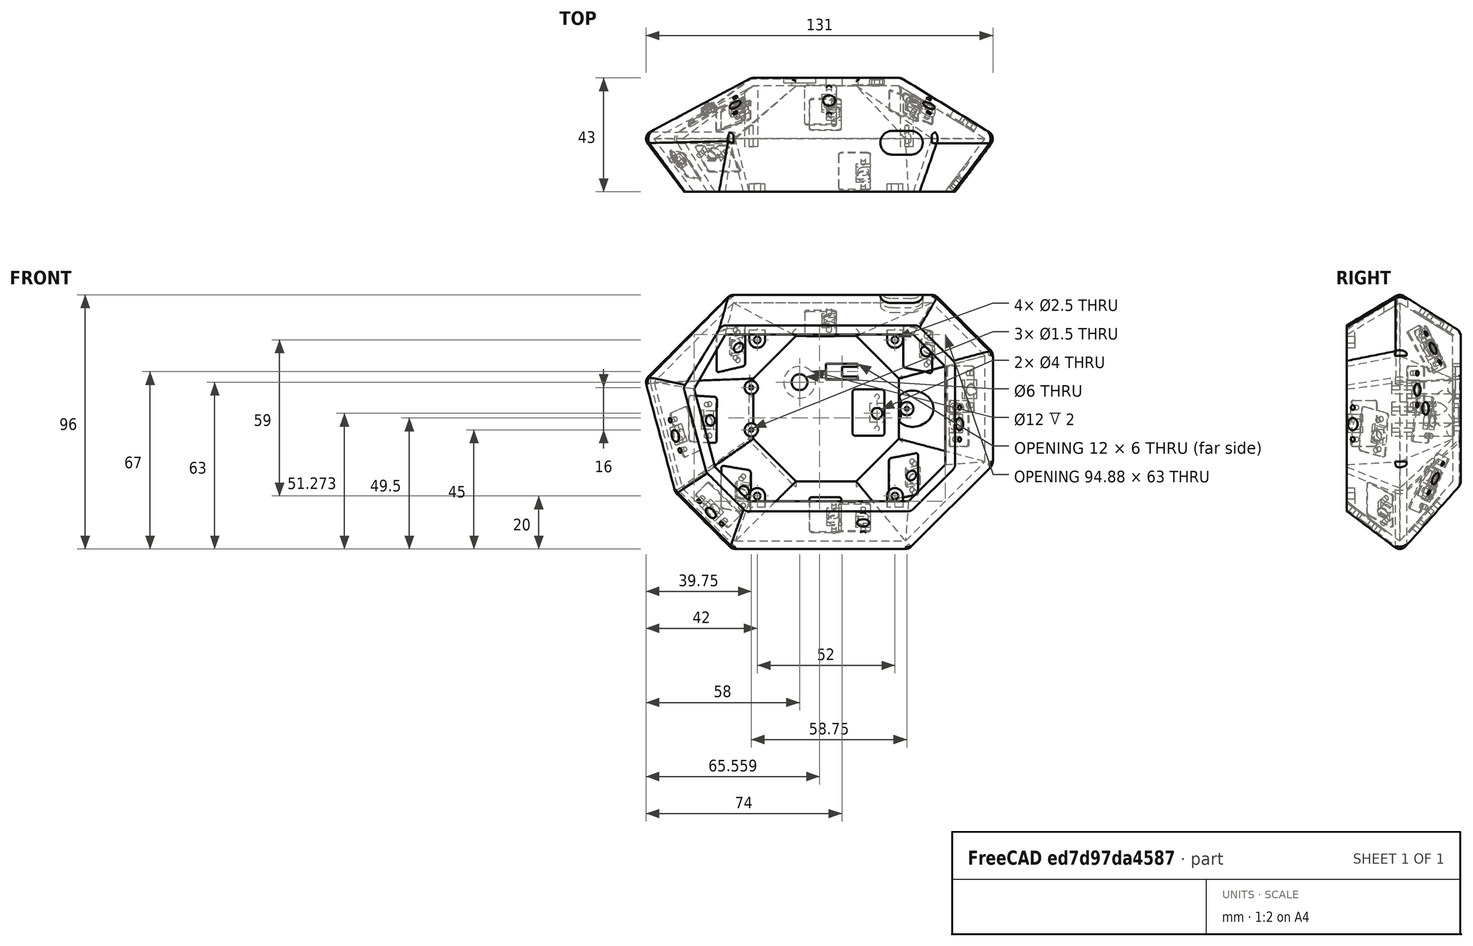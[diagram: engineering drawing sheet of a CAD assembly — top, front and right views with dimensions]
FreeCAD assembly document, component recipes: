
FREECAD ASSEMBLY — COMPONENT RECIPES ("tracker-tut")

This assembly document has 17 components, labeled P0..P16 below (a component is one placed body or linked part). 16 of them carry a construction recipe — the FreeCAD feature program that regenerates the part from scratch, quoted from this document or its linked companion documents; the rest are supplied as boundary geometry only. No exploded tour is included for this assembly.
COMPONENT P0 — recipe-attached ("Tracker final", modeled in this document).
Construction recipe (the document's own serialized feature program — sketch geometry with constraints, then the solid features built on it; lengths are millimeters unless a unit is written):

FEATURE [PartDesign::FeatureBase] BaseFeature
  BaseFeature = -> cut_obj
FEATURE [PartDesign::Plane] DatumPlane002
  AttachmentOffset = pos=(0,0,-17) rot=(0,0,1;0rad)
  Length = 153.4
  MapMode = 5
  Placement = pos=(0,17,3.8e-15) rot=(1,0,0;1.5708rad)
  ResizeMode = 0
  Support = -> [XZ_Plane001]
  Width = 118.409
FEATURE [Sketcher::SketchObject] Sketch003
  FullyConstrained = true
  MapMode = 5
  Placement = pos=(0,17,3.8e-15) rot=(1,0,0;1.5708rad)
  Support = -> [DatumPlane002]
  sketch-geometry (3):
    g0: Circle CenterX=-28.25 CenterY=8 CenterZ=0 NormalX=0 NormalY=0 NormalZ=1 AngleXU=0 Radius=2.5
    g1: Circle CenterX=-28.25 CenterY=-8 CenterZ=0 NormalX=0 NormalY=0 NormalZ=1 AngleXU=0 Radius=2.5
    g2: Circle CenterX=30.5 CenterY=0 CenterZ=0 NormalX=0 NormalY=0 NormalZ=1 AngleXU=0 Radius=2.5
  constraints (9):
    c: PointOnObject(g2,g-1)
    c: DistanceX(g0) = -28.25
    c: DistanceY(g0) = 8
    c: DistanceY(g1,g0) = 16
    c: DistanceX(g0,g2) = 58.75
    c: Equal(g0,g1)
    c: Equal(g1,g2)
    c: Diameter(g0) = 5
    c: Vertical(g1,g0)
FEATURE [PartDesign::Pad] Pad
  BaseFeature = -> BaseFeature
  Direction = (0,-1,-2e-16)
  Length = 18
  Length2 = 10
  Profile = -> Sketch003
  ReferenceAxis = -> Sketch003 [N_Axis]
  Reversed = true
  Type = 2
FEATURE [Sketcher::SketchObject] Sketch004
  FullyConstrained = true
  MapMode = 5
  Placement = pos=(0,17,3.8e-15) rot=(1,0,0;1.5708rad)
  Support = -> [DatumPlane002]
  sketch-geometry (3):
    g0: Circle CenterX=-28.25 CenterY=8 CenterZ=0 NormalX=0 NormalY=0 NormalZ=1 AngleXU=0 Radius=1
    g1: Circle CenterX=-28.25 CenterY=-8 CenterZ=0 NormalX=0 NormalY=0 NormalZ=1 AngleXU=0 Radius=1
    g2: Circle CenterX=30.5 CenterY=0 CenterZ=0 NormalX=0 NormalY=0 NormalZ=1 AngleXU=0 Radius=1
  constraints (9):
    c: PointOnObject(g2,g-1)
    c: DistanceX(g0) = -28.25
    c: DistanceY(g0) = 8
    c: DistanceY(g1,g0) = 16
    c: DistanceX(g2) = 30.5
    c: Equal(g0,g1)
    c: Equal(g0,g2)
    c: Diameter(g0) = 2
    c: Vertical(g1,g0)
FEATURE [PartDesign::Hole] Hole
  BaseFeature = -> Pad
  CustomThreadClearance = 0
  Depth = 8
  DepthType = 0
  Diameter = 1.5
  DrillForDepth = false
  DrillPoint = 1
  DrillPointAngle = 118
  HoleCutCountersinkAngle = 90
  HoleCutCustomValues = false
  HoleCutDepth = 0
  HoleCutDiameter = 6.1
  HoleCutType = 0
  ModelThread = false
  Profile = -> Sketch004
  Tapered = false
  TaperedAngle = 90
  ThreadClass = 0
  ThreadDepth = 8
  ThreadDepthType = 0
  ThreadDirection = 0
  ThreadFit = 0
  ThreadSize = 0
  ThreadType = 0
  Threaded = false
  UseCustomThreadClearance = false
FEATURE [Sketcher::SketchObject] Sketch005
  AttachmentOffset = pos=(0,0,6) rot=(0,0,1;0rad)
  FullyConstrained = true
  MapMode = 5
  Placement = pos=(0,0,6) rot=(0,0,1;0rad)
  Support = -> [XY_Plane001]
  sketch-geometry (4):
    g0: ArcOfCircle CenterX=25 CenterY=18.5 CenterZ=0 NormalX=0 NormalY=0 NormalZ=1 AngleXU=0 Radius=4.5 StartAngle=1.5708 EndAngle=4.71239
    g1: ArcOfCircle CenterX=32 CenterY=18.5 CenterZ=0 NormalX=0 NormalY=0 NormalZ=1 AngleXU=0 Radius=4.5 StartAngle=4.71239 EndAngle=7.85398
    g2: LineSegment StartX=25 StartY=14 StartZ=0 EndX=32 EndY=14 EndZ=0
    g3: LineSegment StartX=32 StartY=23 StartZ=0 EndX=25 EndY=23 EndZ=0
  constraints (10):
    c: Tangent(g0,g2) = -1.5708
    c: Tangent(g2,g1) = -1.5708
    c: Tangent(g1,g3) = -1.5708
    c: Tangent(g3,g0) = -1.5708
    c: Equal(g0,g1)
    c: Horizontal(g2)
    c: DistanceX(g0) = 25
    c: DistanceY(g0) = 18.5
    c: DistanceX(g0,g1) = 7
    c: Radius(g1) = 4.5
FEATURE [PartDesign::Pocket] Pocket
  BaseFeature = -> Hole
  Direction = (0,0,-1)
  Length = 5
  Length2 = 5
  Profile = -> Sketch005
  ReferenceAxis = -> Sketch005 [N_Axis]
  Reversed = true
  Type = 1
FEATURE [Sketcher::SketchObject] Sketch006
  FullyConstrained = true
  MapMode = 5
  Placement = pos=(0,43,0) rot=(0,0.707107,0.707107;3.14159rad)
  Support = -> [Pocket]
  sketch-geometry (1):
    g0: Circle CenterX=10 CenterY=10 CenterZ=0 NormalX=0 NormalY=0 NormalZ=1 AngleXU=0 Radius=6
  constraints (3):
    c: DistanceX(g0) = 10
    c: DistanceY(g0) = 10
    c: Diameter(g0) = 12
FEATURE [PartDesign::Hole] Hole001
  BaseFeature = -> Pocket
  CustomThreadClearance = 0
  Depth = 5
  DepthType = 0
  Diameter = 6
  DrillForDepth = false
  DrillPoint = 1
  DrillPointAngle = 118
  HoleCutCountersinkAngle = 90
  HoleCutCustomValues = false
  HoleCutDepth = 2
  HoleCutDiameter = 12
  HoleCutType = 1
  ModelThread = false
  Profile = -> Sketch006
  Tapered = false
  TaperedAngle = 90
  ThreadClass = 0
  ThreadDepth = 5
  ThreadDepthType = 0
  ThreadDirection = 0
  ThreadFit = 0
  ThreadSize = 0
  ThreadType = 0
  Threaded = false
  UseCustomThreadClearance = false
FEATURE [Sketcher::SketchObject] Sketch007
  FullyConstrained = true
  MapMode = 5
  Placement = pos=(0,43,0) rot=(0,0.707107,0.707107;3.14159rad)
  Support = -> [Hole001]
  sketch-geometry (8):
    g0: LineSegment StartX=-12 StartY=17 StartZ=0 EndX=0 EndY=17 EndZ=0
    g1: LineSegment StartX=0 StartY=17 StartZ=0 EndX=0 EndY=11 EndZ=0
    g2: LineSegment StartX=0 StartY=11 StartZ=0 EndX=-12 EndY=11 EndZ=0
    g3: LineSegment StartX=-12 StartY=11 StartZ=0 EndX=-12 EndY=12.2 EndZ=0
    g4: LineSegment StartX=-12 StartY=12.2 StartZ=0 EndX=-6 EndY=12.2 EndZ=0
    g5: LineSegment StartX=-6 StartY=12.2 StartZ=0 EndX=-6 EndY=15.8 EndZ=0
    g6: LineSegment StartX=-6 StartY=15.8 StartZ=0 EndX=-12 EndY=15.8 EndZ=0
    g7: LineSegment StartX=-12 StartY=15.8 StartZ=0 EndX=-12 EndY=17 EndZ=0
  constraints (24):
    c: Horizontal(g0)
    c: Coincident(g0,g1)
    c: Coincident(g1,g2)
    c: Horizontal(g2)
    c: Coincident(g2,g3)
    c: Vertical(g3)
    c: Coincident(g3,g4)
    c: Horizontal(g4)
    c: Coincident(g4,g5)
    c: Vertical(g5)
    c: Coincident(g5,g6)
    c: Horizontal(g6)
    c: Coincident(g6,g7)
    c: Coincident(g7,g0)
    c: Vertical(g7)
    c: Vertical(g1)
    c: DistanceY(g1,g1) = 6
    c: Equal(g7,g3)
    c: DistanceY(g3,g3) = 1.2
    c: DistanceX(g4,g1) = 6
    c: DistanceX(g2,g2) = 12
    c: Vertical(g3,g6)
    c: DistanceX(g1) = 0
    c: DistanceY(g1) = 11
FEATURE [PartDesign::Pocket] Pocket001
  BaseFeature = -> Hole001
  Direction = (0,-1,-2e-16)
  Length = 5
  Length2 = 5
  Profile = -> Sketch007
  ReferenceAxis = -> Sketch007 [N_Axis]
  Type = 0
FEATURE [Sketcher::SketchObject] Sketch008
  FullyConstrained = true
  MapMode = 5
  Placement = pos=(0,0,0) rot=(1,0,0;1.5708rad)
  Support = -> [XZ_Plane001]
  sketch-geometry (10):
    g0: ArcOfCircle CenterX=-26 CenterY=26 CenterZ=0 NormalX=0 NormalY=0 NormalZ=1 AngleXU=0 Radius=3 StartAngle=3.14159 EndAngle=6.28319
    g1: LineSegment StartX=-29 StartY=26 StartZ=0 EndX=-29 EndY=31 EndZ=0
    g2: LineSegment StartX=-29 StartY=31 StartZ=0 EndX=-23 EndY=31 EndZ=0
    g3: LineSegment StartX=-23 StartY=31 StartZ=0 EndX=-23 EndY=26 EndZ=0
    g4: Circle CenterX=-26 CenterY=26 CenterZ=0 NormalX=0 NormalY=0 NormalZ=1 AngleXU=0 Radius=1.25
    g5: Circle CenterX=-26 CenterY=-33 CenterZ=0 NormalX=0 NormalY=0 NormalZ=1 AngleXU=0 Radius=1.25
    g6: ArcOfCircle CenterX=-26 CenterY=-33 CenterZ=0 NormalX=0 NormalY=0 NormalZ=1 AngleXU=0 Radius=3 StartAngle=5.6e-15 EndAngle=3.14159
    g7: LineSegment StartX=-29 StartY=-33 StartZ=0 EndX=-29 EndY=-38 EndZ=0
    g8: LineSegment StartX=-29 StartY=-38 StartZ=0 EndX=-23 EndY=-38 EndZ=0
    g9: LineSegment StartX=-23 StartY=-38 StartZ=0 EndX=-23 EndY=-33 EndZ=0
  constraints (26):
    c: Vertical(g1)
    c: Coincident(g1,g2)
    c: Horizontal(g2)
    c: Coincident(g2,g3)
    c: Vertical(g3)
    c: Tangent(g0,g3) = 1.5708
    c: Tangent(g0,g1) = 1.5708
    c: Coincident(g4,g0)
    c: Diameter(g4) = 2.5
    c: Radius(g0) = 3
    c: DistanceX(g0) = -26
    c: DistanceY(g0) = 26
    c: DistanceY(g0,g2) = 5
    c: Coincident(g6,g5)
    c: Coincident(g7,g8)
    c: Horizontal(g8)
    c: Coincident(g8,g9)
    c: Equal(g5,g4)
    c: Equal(g6,g0)
    c: Vertical(g7)
    c: Vertical(g9)
    c: Tangent(g6,g9) = -1.5708
    c: Vertical(g5,g0)
    c: DistanceY(g5) = -33
    c: Tangent(g6,g7) = -1.5708
    c: DistanceY(g8,g5) = 5
FEATURE [PartDesign::Pad] Pad001
  BaseFeature = -> Pocket001
  Direction = (0,-1,-2e-16)
  Length = 3
  Length2 = 10
  Profile = -> Sketch008
  ReferenceAxis = -> Sketch008 [N_Axis]
  Refine = true
  Reversed = true
  Type = 0
FEATURE [PartDesign::Mirrored] Mirrored
  BaseFeature = -> Pad001
  MirrorPlane = -> Sketch008 [V_Axis]
  Originals = -> [Pad001]
  Refine = true
FEATURE [PartDesign::Fillet] Fillet
  Base = -> Mirrored [Edge455]
  BaseFeature = -> Mirrored
  Radius = 5
  SupportTransform = false
  UseAllEdges = false
FEATURE [PartDesign::Body] Body001  label="Tracker final"
  BaseFeature = -> cut_obj
  Group = -> [BaseFeature,DatumPlane002,Sketch003,Pad,Sketch004,Hole,Sketch005,Pocket,Sketch006,Hole001,Sketch007,Pocket001,Sketch008,Pad001,Mirrored,Fillet]
  Origin = -> Origin001
  Tip = -> Fillet
COMPONENT P1 — geometry summary ("tracker-mainboard"; no construction recipe available for this part):
  bounding box: 71.5 x 44.8 x 11.5 mm
  tessellated surface: 104,766 triangles
  volume: 4982 mm^3 (13% of its bounding box)
COMPONENT P2 — recipe-attached ("sensor", a linked part whose construction recipe lives in a companion FreeCAD document of the same project; that document's serialized recipe follows).
Construction recipe (the companion document, serialized — sketch geometry with constraints, then the solid features built on it; lengths are millimeters unless a unit is written):

FCSTD DOCUMENT  (FreeCAD 0.20R29603 (Git))
Label: sensor-PCB
License: All rights reserved
LicenseURL: http://en.wikipedia.org/wiki/All_rights_reserved
objects: Part::Feature×21, App::Part×16, App::Link×15, Part::Compound2×3, PartDesign::SubShapeBinder×2, PartDesign::CoordinateSystem×2, App::FeaturePython×1, PartDesign::Body×1
note: 26 computed .brp shape members not serialized (recipe doc carries the construction recipe); baked Part::Feature solids carry a one-line shape summary decoded from their .brp

FEATURE [App::FeaturePython] Constraints  # WARN: FeaturePython — macro-defined, semantics opaque (R4)
  _Version = 1
FEATURE [App::Link] Link  label="ball001"
  LinkPlacement = pos=(0,0.5,0.125) rot=(0,0,1;0rad)
  LinkedObject = -> Solid002
  Placement = pos=(0,0.5,0.125) rot=(0,0,1;0rad)
FEATURE [App::Link] Link001  label="ball002"
  LinkPlacement = pos=(0.5,0.5,0.125) rot=(0,0,1;0rad)
  LinkedObject = -> Solid002
  Placement = pos=(0.5,0.5,0.125) rot=(0,0,1;0rad)
FEATURE [App::Link] Link002  label="ball003"
  LinkPlacement = pos=(-0.5,0,0.125) rot=(0,0,1;0rad)
  LinkedObject = -> Solid002
  Placement = pos=(-0.5,0,0.125) rot=(0,0,1;0rad)
FEATURE [App::Link] Link003  label="ball004"
  LinkPlacement = pos=(0,0,0.125) rot=(0,0,1;0rad)
  LinkedObject = -> Solid002
  Placement = pos=(0,0,0.125) rot=(0,0,1;0rad)
FEATURE [App::Link] Link004  label="ball005"
  LinkPlacement = pos=(0.5,0,0.125) rot=(0,0,1;0rad)
  LinkedObject = -> Solid002
  Placement = pos=(0.5,0,0.125) rot=(0,0,1;0rad)
FEATURE [App::Link] Link005  label="ball006"
  LinkPlacement = pos=(-0.5,-0.5,0.125) rot=(0,0,1;0rad)
  LinkedObject = -> Solid002
  Placement = pos=(-0.5,-0.5,0.125) rot=(0,0,1;0rad)
FEATURE [App::Link] Link006  label="ball007"
  LinkPlacement = pos=(0,-0.5,0.125) rot=(0,0,1;0rad)
  LinkedObject = -> Solid002
  Placement = pos=(0,-0.5,0.125) rot=(0,0,1;0rad)
FEATURE [App::Link] Link007  label="ball008"
  LinkPlacement = pos=(0.5,-0.5,0.125) rot=(0,0,1;0rad)
  LinkedObject = -> Solid002
  Placement = pos=(0.5,-0.5,0.125) rot=(0,0,1;0rad)
FEATURE [App::Link] Link008  label="Terminal001"
  LinkPlacement = pos=(1.2,0.45,0) rot=(0,0,1;3.14159rad)
  LinkedObject = -> Part004
  Placement = pos=(1.2,0.45,0) rot=(0,0,1;3.14159rad)
FEATURE [App::Link] Link009  label="68X1XX183X22_Pin_TOP001"
  LinkPlacement = pos=(-0.4,1.05,-0.045) rot=(0,0,1;1.5708rad)
  LinkedObject = -> Solid010
  Placement = pos=(-0.4,1.05,-0.045) rot=(0,0,1;1.5708rad)
FEATURE [App::Link] Link010  label="68X1XX183X22_Pin_TOP002"
  LinkPlacement = pos=(0.6,1.05,-0.045) rot=(0,0,1;1.5708rad)
  LinkedObject = -> Solid010
  Placement = pos=(0.6,1.05,-0.045) rot=(0,0,1;1.5708rad)
FEATURE [App::Link] Link011  label="68X1XX183X22_Pin_TOP003"
  LinkPlacement = pos=(1.6,1.05,-0.045) rot=(0,0,1;1.5708rad)
  LinkedObject = -> Solid010
  Placement = pos=(1.6,1.05,-0.045) rot=(0,0,1;1.5708rad)
FEATURE [App::Link] Link012  label="pin001"
  LinkPlacement = pos=(0.375,3e-16,-3e-16) rot=(0,0,1;3.14159rad)
  LinkedObject = -> Solid019
  Placement = pos=(0.375,3e-16,-3e-16) rot=(0,0,1;3.14159rad)
FEATURE [App::Link] Link013  label="1x0.5x0.5x0.026"
  LinkPlacement = pos=(4.25098,5.93,0) rot=(0,0,-1;1.5708rad)
  LinkedObject = -> Part011
  Placement = pos=(4.25098,5.93,0) rot=(0,0,-1;1.5708rad)
FEATURE [App::Link] Link014  label="1x0.5x0.5x0.027"
  LinkPlacement = pos=(4.88605,11.5101,0) rot=(0,0,1;0rad)
  LinkedObject = -> Part011
  Placement = pos=(4.88605,11.5101,0) rot=(0,0,1;0rad)
FEATURE [App::Part] Part013  label="C2"
  Group = -> [Link013]
  Origin = -> Origin013
FEATURE [App::Part] Part015  label="C1"
  Group = -> [Link014]
  Origin = -> Origin015
FEATURE [Part::Feature] Shell  label="Open_CASCADE_STEP_translator_6.8_1.1"
  Placement = pos=(-0.81,-0.79,0) rot=(0,0,1;0rad)
  shape: bbox 0.2025 x 0.2025 x 2e-07 mm, 1 faces, 0 solids (baked)
FEATURE [Part::Feature] Solid  label="Open CASCADE STEP translator 6.8 2.1.1"
  Placement = pos=(0,0,-1.54144) rot=(0,0,1;0rad)
  shape: bbox 11.5 x 17 x 1.541 mm, 14 faces (baked)
FEATURE [App::Part] Part  label="Board"
  Group = -> [Solid]
  Origin = -> Origin
FEATURE [Part::Feature] Solid001  label="Open_CASCADE_STEP_translator_6.8_1.2.1"
  shape: bbox 1.62 x 1.58 x 0.475 mm, 8 faces (baked)
FEATURE [App::Part] Part001  label="Body"
  Group = -> [Solid001]
  Origin = -> Origin001
  Placement = pos=(-0.81,-0.79,0) rot=(0,0,1;0rad)
FEATURE [Part::Feature] Solid002  label="ball"
  Placement = pos=(-0.5,0.5,0.125) rot=(0,0,1;0rad)
  shape: bbox 0.25 x 0.25 x 0.25 mm, 1 faces (baked)
FEATURE [App::Part] Part002  label="5833252656"
  Group = -> [Shell,Part001,Solid002,Link,Link001,Link002,Link003,Link004,Link005,Link006,Link007]
  Origin = -> Origin002
  Placement = pos=(4.878,8.47,0) rot=(0,0,1;1.5708rad)
FEATURE [App::Part] Part003  label="U1"
  Group = -> [Part002]
  Origin = -> Origin003
FEATURE [Part::Feature] Solid003  label="Mid_Body"
  Placement = pos=(-1.2,-0.45,0) rot=(0,0,1;0rad)
  shape: bbox 2.28 x 0.9 x 0.48 mm, 6 faces (baked)
FEATURE [Part::Feature] Solid004  label="Open_CASCADE_STEP_translator_6.8_3.2.1"
  shape: bbox 0.7 x 0.9 x 0.6 mm, 10 faces (baked)
FEATURE [App::Part] Part004  label="Terminal"
  Group = -> [Solid004]
  Origin = -> Origin004
  Placement = pos=(-1.2,-0.45,0) rot=(0,0,1;0rad)
FEATURE [Part::Feature] Solid005  label="Mark"
  Placement = pos=(-0.5,-0.45,0.54) rot=(0,0,1;0rad)
  shape: bbox 1 x 0.9 x 0.06 mm, 6 faces (baked)
FEATURE [App::Part] Part005  label="5983538608"
  Group = -> [Solid003,Part004,Link008,Solid005]
  Origin = -> Origin005
  Placement = pos=(5.6,5.5,0) rot=(0,0,1;1.5708rad)
FEATURE [App::Part] Part006  label="R1"
  Group = -> [Part005]
  Origin = -> Origin006
FEATURE [Part::Feature] Solid006  label="68x109183x22"
  shape: bbox 7.5 x 3.1 x 1.2 mm, 237 faces (baked)
FEATURE [Part::Feature] Solid007  label="68x109183x22_Actuator"
  Placement = pos=(-1.67e-13,-2,5e-15) rot=(1,0,0;3.14159rad)
  shape: bbox 10.2 x 3.8 x 1.1 mm, 117 faces (baked)
FEATURE [Part::Feature] Solid008  label="68X1xx183x22_Solder_Pad2"
  Placement = pos=(2.8,-0.25,-0.02) rot=(0,0,-1;1.5708rad)
  shape: bbox 2 x 2.5 x 1.24 mm, 61 faces (baked)
FEATURE [Part::Feature] Solid009  label="68X1XX183X22_Solder_Pad"
  Placement = pos=(-2.8,-0.25,-0.02) rot=(0.707107,-0.707107,0;3.14159rad)
  shape: bbox 2 x 2.5 x 1.24 mm, 61 faces (baked)
FEATURE [Part::Feature] Solid010  label="68X1XX183X22_Pin_TOP"
  Placement = pos=(-1.4,1.05,-0.045) rot=(0,0,1;1.5708rad)
  shape: bbox 0.2 x 3.097 x 1.15 mm, 38 faces (baked)
FEATURE [App::Part] Part007  label="686104183422"
  Group = -> [Solid006,Solid007,Solid008,Solid009,Solid010,Link009,Link010,Link011]
  Origin = -> Origin007
  Placement = pos=(8.95005,8.49992,0.640001) rot=(0.707107,-0.707107,0;3.14159rad)
FEATURE [App::Part] Part008  label="J1"
  Group = -> [Part007]
  Origin = -> Origin008
FEATURE [Part::Feature] Solid011
  shape: bbox 4.436 x 3.936 x 1 mm, 6 faces (baked)
FEATURE [Part::Feature] Solid012
  shape: bbox 4.7 x 4.4 x 0.3 mm, 18 faces (baked)
FEATURE [Part::Feature] Solid013
  shape: bbox 4.5 x 4 x 0.4 mm, 21 faces (baked)
FEATURE [Part::Compound2] Compound  label="body"
  Links = -> [Solid011,Solid012,Solid013]
  Placement = pos=(-0.585529,0.102898,-0.610932) rot=(0,0,1;0rad)
FEATURE [Part::Feature] Solid014
  shape: bbox 0.8 x 1.1 x 0.3 mm, 6 faces (baked)
FEATURE [Part::Feature] Solid015
  shape: bbox 0.8 x 3.7 x 0.65 mm, 10 faces (baked)
FEATURE [Part::Compound2] Compound001  label="footA"
  Links = -> [Solid014,Solid015]
  Placement = pos=(-3.28553,0.102898,-1.16041) rot=(0.57735,0.57735,0.57735;2.0944rad)
FEATURE [Part::Feature] Solid016
  shape: bbox 0.8 x 1.1 x 0.3 mm, 6 faces (baked)
FEATURE [Part::Feature] Solid017
  shape: bbox 1.5 x 3.7 x 0.65 mm, 14 faces (baked)
FEATURE [Part::Compound2] Compound002  label="footB"
  Links = -> [Solid016,Solid017]
  Placement = pos=(2.11447,0.102898,-1.16093) rot=(0.57735,-0.57735,-0.57735;2.0944rad)
FEATURE [App::Part] Part009  label="BPW34"
  Group = -> [Compound,Compound001,Compound002,Solid012,Solid013,Solid011,Solid014,Solid015,Solid017,Solid016]
  Origin = -> Origin009
  Placement = pos=(2.39719,9.08559,-2.14144) rot=(0.707107,0.707107,0;3.14159rad)
FEATURE [App::Part] Part010  label="D1"
  Group = -> [Part009]
  Origin = -> Origin010
FEATURE [Part::Feature] Solid018  label="base"
  shape: bbox 0.5 x 0.5 x 0.5 mm, 10 faces (baked)
FEATURE [Part::Feature] Solid019  label="pin"
  Placement = pos=(-0.375,0,0) rot=(0,0,1;0rad)
  shape: bbox 0.25 x 0.5 x 0.5 mm, 18 faces (baked)
FEATURE [App::Part] Part011  label="1x0.5x0.5x0.25"
  Group = -> [Solid018,Solid019,Link012]
  Origin = -> Origin011
  Placement = pos=(4.88605,10.3671,0) rot=(0,0,1;0rad)
FEATURE [App::Part] Part012  label="C3"
  Group = -> [Part011]
  Origin = -> Origin012
FEATURE [PartDesign::SubShapeBinder] Binder001
  BindCopyOnChange = 0
  BindMode = 0
  ClaimChildren = false
  Context = -> Part014 [Sensor_shape.Binder001.]
  Fuse = false
  MakeFace = true
  OffsetFill = false
  OffsetIntersection = false
  OffsetJoinType = 0
  OffsetOpenResult = false
  PartialLoad = false
  Relative = true
  Support = -> [Part[Solid.Edge11,Solid.Edge10,Solid.Edge5,Solid.Edge3,Solid.Edge23,Solid.Edge22,Solid.Edge17,Solid.Edge16]]
  _Version = 2
FEATURE [PartDesign::SubShapeBinder] Binder
  BindCopyOnChange = 0
  BindMode = 0
  ClaimChildren = false
  Context = -> Part014 [Sensor_shape.Binder.]
  Fuse = false
  MakeFace = true
  OffsetFill = false
  OffsetIntersection = false
  OffsetJoinType = 0
  OffsetOpenResult = false
  PartialLoad = false
  Relative = true
  Support = -> [Part010[Part009.Compound.Edge96,Part009.Compound.Edge94,Part009.Compound.Edge92,Part009.Compound.Edge90]]
  _Version = 2
FEATURE [PartDesign::CoordinateSystem] Local_CS  label="LCS-Base"
  AttacherType = Attacher::AttachEngine3D
  AttachmentOffset = pos=(0,0,-4) rot=(1,0,0;3.14159rad)
  MapMode = 45
  Placement = pos=(5.75,8.5,-4) rot=(1,0,0;3.14159rad)
  Support = -> [Binder001]
FEATURE [PartDesign::CoordinateSystem] Local_CS001  label="LCS-Diode"
  AttacherType = Attacher::AttachEngine3D
  AttachmentOffset = pos=(0,0,0) rot=(1,0,0;3.14159rad)
  MapMode = 45
  Placement = pos=(2.50009,8.75006,-3.21051) rot=(1,0,0;3.14159rad)
  Support = -> [Binder]
FEATURE [PartDesign::Body] Sensor_shape  label="Sensor-shape"
  Group = -> [Binder001,Binder,Local_CS,Local_CS001]
  Origin = -> Origin016
FEATURE [App::Part] Part014  label="sensor"
  Group = -> [Part,Part003,Part006,Part008,Part010,Part012,Part013,Part015,Sensor_shape]
  Origin = -> Origin014
  Placement = pos=(-2.5,8.75,-3.2) rot=(1,0,0;3.14159rad)
COMPONENT P3 — same part as P2; its construction recipe is shown at P2.
COMPONENT P4 — same part as P2; its construction recipe is shown at P2.
COMPONENT P5 — same part as P2; its construction recipe is shown at P2.
COMPONENT P6 — same part as P2; its construction recipe is shown at P2.
COMPONENT P7 — same part as P2; its construction recipe is shown at P2.
COMPONENT P8 — same part as P2; its construction recipe is shown at P2.
COMPONENT P9 — same part as P2; its construction recipe is shown at P2.
COMPONENT P10 — same part as P2; its construction recipe is shown at P2.
COMPONENT P11 — same part as P2; its construction recipe is shown at P2.
COMPONENT P12 — same part as P2; its construction recipe is shown at P2.
COMPONENT P13 — same part as P2; its construction recipe is shown at P2.
COMPONENT P14 — same part as P2; its construction recipe is shown at P2.
COMPONENT P15 — recipe-attached ("stamp", modeled in this document).
Construction recipe (the document's own serialized feature program — sketch geometry with constraints, then the solid features built on it; lengths are millimeters unless a unit is written):

FEATURE [Sketcher::SketchObject] Sketch
  FullyConstrained = true
  MapMode = 5
  Support = -> [XY_Plane]
  sketch-geometry (8):
    g0: LineSegment StartX=-42 StartY=22 StartZ=0 EndX=-29 EndY=35 EndZ=0
    g1: LineSegment StartX=-29 StartY=35 StartZ=0 EndX=31.1443 EndY=35 EndZ=0
    g2: LineSegment StartX=31.1443 StartY=35 StartZ=0 EndX=45 EndY=21.1443 EndZ=0
    g3: LineSegment StartX=45 StartY=21.1443 StartZ=0 EndX=45 EndY=-16 EndZ=0
    g4: LineSegment StartX=45 StartY=-16 StartZ=0 EndX=33 EndY=-28 EndZ=0
    g5: LineSegment StartX=33 StartY=-28 StartZ=0 EndX=-38 EndY=-28 EndZ=0
    g6: LineSegment StartX=-38 StartY=-28 StartZ=0 EndX=-49.8827 EndY=-7.41858 EndZ=0
    g7: LineSegment StartX=-49.8827 StartY=-7.41858 StartZ=0 EndX=-42 EndY=22 EndZ=0
  constraints (24):
    c: Coincident(g0,g1)
    c: Horizontal(g1)
    c: Coincident(g1,g2)
    c: Coincident(g2,g3)
    c: Vertical(g3)
    c: Coincident(g3,g4)
    c: Coincident(g4,g5)
    c: Horizontal(g5)
    c: Coincident(g5,g6)
    c: Coincident(g6,g7)
    c: Coincident(g7,g0)
    c: DistanceX(g0) = -42
    c: DistanceY(g0) = 22
    c: DistanceX(g2) = 45
    c: DistanceY(g2) = 21.1443
    c: DistanceY(g3) = -16
    c: Angle(g0,g1) = 2.35619
    c: Angle(g2,g3) = 2.35619
    c: Angle(g3,g4) = 2.35619
    c: Angle(g5,g6) = 2.0944
    c: DistanceX(g5) = -38
    c: DistanceY(g0) = 35
    c: DistanceY(g5) = -28
    c: Angle(g6,g7) = 2.35619
FEATURE [PartDesign::Plane] DatumPlane
  AttachmentOffset = pos=(0,0,20) rot=(0,0,1;0rad)
  Length = 153.4
  MapMode = 5
  Placement = pos=(0,0,20) rot=(0,0,1;0rad)
  ResizeMode = 0
  Support = -> [XY_Plane]
  Width = 118.403
FEATURE [PartDesign::Plane] DatumPlane001
  AttachmentOffset = pos=(0,0,20) rot=(0,0,1;0rad)
  Length = 153.4
  MapMode = 5
  Placement = pos=(0,0,40) rot=(0,0,1;0rad)
  ResizeMode = 0
  Support = -> [DatumPlane]
  Width = 118.403
FEATURE [Sketcher::SketchObject] Sketch001
  FullyConstrained = true
  MapMode = 5
  Placement = pos=(0,0,20) rot=(0,0,1;0rad)
  Support = -> [DatumPlane]
  sketch-geometry (8):
    g0: LineSegment StartX=-34.282 StartY=50 StartZ=0 EndX=30 EndY=50 EndZ=0
    g1: LineSegment StartX=30 StartY=50 StartZ=0 EndX=60 EndY=20 EndZ=0
    g2: LineSegment StartX=60 StartY=20 StartZ=0 EndX=60 EndY=-20 EndZ=0
    g3: LineSegment StartX=60 StartY=-20 StartZ=0 EndX=40 EndY=-40 EndZ=0
    g4: LineSegment StartX=40 StartY=-40 StartZ=0 EndX=-35 EndY=-40 EndZ=0
    g5: LineSegment StartX=-35 StartY=-40 StartZ=0 EndX=-65 EndY=-10 EndZ=0
    g6: LineSegment StartX=-65 StartY=-10 StartZ=0 EndX=-54.282 EndY=30 EndZ=0
    g7: LineSegment StartX=-54.282 StartY=30 StartZ=0 EndX=-34.282 EndY=50 EndZ=0
  constraints (24):
    c: Horizontal(g0)
    c: Coincident(g0,g1)
    c: Coincident(g1,g2)
    c: Vertical(g2)
    c: Coincident(g2,g3)
    c: Coincident(g3,g4)
    c: Horizontal(g4)
    c: Coincident(g4,g5)
    c: Coincident(g5,g6)
    c: Coincident(g6,g7)
    c: Coincident(g7,g0)
    c: Angle(g2,g3) = 2.35619
    c: Angle(g1,g2) = 2.35619
    c: Angle(g6,g7) = 2.61799
    c: DistanceY(g4) = -40
    c: DistanceX(g4) = -35
    c: Angle(g4,g5) = 2.35619
    c: DistanceX(g5) = -65
    c: DistanceX(g2) = 60
    c: DistanceY(g2) = -20
    c: DistanceY(g1) = 20
    c: DistanceY(g0) = 50
    c: DistanceY(g6) = 30
    c: Angle(g5,g6) = 2.0944
FEATURE [Sketcher::SketchObject] Sketch002
  FullyConstrained = true
  MapMode = 5
  Placement = pos=(0,0,40) rot=(0,0,1;0rad)
  Support = -> [DatumPlane001]
  sketch-geometry (9):
    g0: LineSegment StartX=27.5 StartY=11.3909 StartZ=0 EndX=11.3909 EndY=27.5 EndZ=0
    g1: LineSegment StartX=11.3909 StartY=27.5 StartZ=0 EndX=-11.3909 EndY=27.5 EndZ=0
    g2: LineSegment StartX=-11.3909 StartY=27.5 StartZ=0 EndX=-27.5 EndY=11.3909 EndZ=0
    g3: LineSegment StartX=-27.5 StartY=11.3909 StartZ=0 EndX=-27.5 EndY=-11.3909 EndZ=0
    g4: LineSegment StartX=-27.5 StartY=-11.3909 StartZ=0 EndX=-11.3909 EndY=-27.5 EndZ=0
    g5: LineSegment StartX=-11.3909 StartY=-27.5 StartZ=0 EndX=11.3909 EndY=-27.5 EndZ=0
    g6: LineSegment StartX=11.3909 StartY=-27.5 StartZ=0 EndX=27.5 EndY=-11.3909 EndZ=0
    g7: LineSegment StartX=27.5 StartY=-11.3909 StartZ=0 EndX=27.5 EndY=11.3909 EndZ=0
    g8: Circle CenterX=0 CenterY=0 CenterZ=0 NormalX=0 NormalY=0 NormalZ=1 AngleXU=0 Radius=29.7658
  constraints (20):
    c: Coincident(g0,g1)
    c: Coincident(g1,g2)
    c: Coincident(g2,g3)
    c: Coincident(g3,g4)
    c: Coincident(g4,g5)
    c: Coincident(g5,g6)
    c: Coincident(g6,g7)
    c: Coincident(g7,g0)
    c: Equal(g0, g1-g7) x7
    c: PointOnObject(g0,g8)
    c: PointOnObject(g1,g8)
    c: PointOnObject(g2,g8)
    c: PointOnObject(g3,g8)
    c: PointOnObject(g4,g8)
    c: PointOnObject(g5,g8)
    c: PointOnObject(g6,g8)
    c: PointOnObject(g7,g8)
    c: Coincident(g8,g-1)
    c: DistanceX(g2,g0) = 55
    c: Vertical(g3)
FEATURE [PartDesign::AdditiveLoft] AdditiveLoft
  Closed = false
  Profile = -> Sketch
  Ruled = true
  Sections = -> [Sketch001,Sketch002]
FEATURE [PartDesign::Thickness] Thickness
  Base = -> AdditiveLoft [Face1]
  BaseFeature = -> AdditiveLoft
  Intersection = false
  Join = 0
  Mode = 0
  SupportTransform = false
  Value = 3
FEATURE [PartDesign::Point] p_surf0
  AttacherType = Attacher::AttachEnginePoint
  Placement = pos=(55.6643,9.21912,-8.57316) rot=(0,0,1;0rad)
FEATURE [PartDesign::Point] p_norm0
  AttacherType = Attacher::AttachEnginePoint
  Placement = pos=(56.4643,8.61912,-8.57316) rot=(0,0,1;0rad)
FEATURE [PartDesign::Point] p_aux0
  AttacherType = Attacher::AttachEnginePoint
  Placement = pos=(54.6643,9.21912,-8.57316) rot=(0,0,1;0rad)
FEATURE [PartDesign::CoordinateSystem] s_lcs0
  AttacherType = Attacher::AttachEngine3D
  MapMode = 47
  Placement = pos=(55.6643,9.21912,-8.57316) rot=(-0.333333,0.666667,-0.666667;2.49809rad)
  Support = -> [p_surf0,p_norm0,p_aux0]
FEATURE [PartDesign::Point] p_surf1
  AttacherType = Attacher::AttachEnginePoint
  Placement = pos=(-55.5034,8.89833,-9.68447) rot=(0,0,1;0rad)
FEATURE [PartDesign::Point] p_norm1
  AttacherType = Attacher::AttachEnginePoint
  Placement = pos=(-56.296,8.32669,-9.89683) rot=(0,0,1;0rad)
FEATURE [PartDesign::Point] p_aux1
  AttacherType = Attacher::AttachEnginePoint
  Placement = pos=(-56.5034,8.89833,-9.68447) rot=(0,0,1;0rad)
FEATURE [PartDesign::CoordinateSystem] s_lcs1
  AttacherType = Attacher::AttachEngine3D
  MapMode = 47
  Placement = pos=(-55.5034,8.89833,-9.68447) rot=(0.270563,0.790424,-0.549568;3.88381rad)
  Support = -> [p_surf1,p_norm1,p_aux1]
FEATURE [PartDesign::Point] p_surf2
  AttacherType = Attacher::AttachEnginePoint
  Placement = pos=(-2.11464,34.2418,34.6366) rot=(0,0,1;0rad)
FEATURE [PartDesign::Point] p_norm2
  AttacherType = Attacher::AttachEnginePoint
  Placement = pos=(-2.11464,34.7718,35.4846) rot=(0,0,1;0rad)
FEATURE [PartDesign::Point] p_aux2
  AttacherType = Attacher::AttachEnginePoint
  Placement = pos=(-3.11464,34.2418,34.6366) rot=(0,0,1;0rad)
FEATURE [PartDesign::CoordinateSystem] s_lcs2
  AttacherType = Attacher::AttachEngine3D
  MapMode = 47
  Placement = pos=(-2.11464,34.2418,34.6366) rot=(0,0.275683,0.961249;3.14159rad)
  Support = -> [p_surf2,p_norm2,p_aux2]
FEATURE [PartDesign::Point] p_surf3
  AttacherType = Attacher::AttachEnginePoint
  Placement = pos=(-37.2571,31.4856,23.8863) rot=(0,0,1;0rad)
FEATURE [PartDesign::Point] p_norm3
  AttacherType = Attacher::AttachEnginePoint
  Placement = pos=(-37.6931,32.2729,24.3223) rot=(0,0,1;0rad)
FEATURE [PartDesign::Point] p_aux3
  AttacherType = Attacher::AttachEnginePoint
  Placement = pos=(-38.2571,31.4856,23.8863) rot=(0,0,1;0rad)
FEATURE [PartDesign::CoordinateSystem] s_lcs3
  AttacherType = Attacher::AttachEngine3D
  MapMode = 47
  Placement = pos=(-37.2571,31.4856,23.8863) rot=(-0.193969,0.498039,0.845182;3.36921rad)
  Support = -> [p_surf3,p_norm3,p_aux3]
FEATURE [PartDesign::Point] p_surf4
  AttacherType = Attacher::AttachEnginePoint
  Placement = pos=(-35.1225,31.3167,-31.4979) rot=(0,0,1;0rad)
FEATURE [PartDesign::Point] p_norm4
  AttacherType = Attacher::AttachEnginePoint
  Placement = pos=(-35.4964,32.1654,-31.8719) rot=(0,0,1;0rad)
FEATURE [PartDesign::Point] p_aux4
  AttacherType = Attacher::AttachEnginePoint
  Placement = pos=(-36.1225,31.3167,-31.4979) rot=(0,0,1;0rad)
FEATURE [PartDesign::CoordinateSystem] s_lcs4
  AttacherType = Attacher::AttachEngine3D
  MapMode = 47
  Placement = pos=(-35.1225,31.3167,-31.4979) rot=(-0.105392,0.832954,0.543213;3.46204rad)
  Support = -> [p_surf4,p_norm4,p_aux4]
FEATURE [PartDesign::Point] p_surf5
  AttacherType = Attacher::AttachEnginePoint
  Placement = pos=(16.0047,43,-1.47684) rot=(0,0,1;0rad)
FEATURE [PartDesign::Point] p_norm5
  AttacherType = Attacher::AttachEnginePoint
  Placement = pos=(16.0047,44,-1.47684) rot=(0,0,1;0rad)
FEATURE [PartDesign::Point] p_aux5
  AttacherType = Attacher::AttachEnginePoint
  Placement = pos=(15.0047,43,-1.47684) rot=(0,0,1;0rad)
FEATURE [PartDesign::CoordinateSystem] s_lcs5
  AttacherType = Attacher::AttachEngine3D
  MapMode = 47
  Placement = pos=(16.0047,43,-1.47684) rot=(0,0.707107,0.707107;3.14159rad)
  Support = -> [p_surf5,p_norm5,p_aux5]
FEATURE [PartDesign::Point] p_surf6
  AttacherType = Attacher::AttachEnginePoint
  Placement = pos=(-0.26869,31.198,-41.9178) rot=(0,0,1;0rad)
FEATURE [PartDesign::Point] p_norm6
  AttacherType = Attacher::AttachEnginePoint
  Placement = pos=(-0.26869,31.9454,-42.5822) rot=(0,0,1;0rad)
FEATURE [PartDesign::Point] p_aux6
  AttacherType = Attacher::AttachEnginePoint
  Placement = pos=(-1.26869,31.198,-41.9178) rot=(0,0,1;0rad)
FEATURE [PartDesign::CoordinateSystem] s_lcs6
  AttacherType = Attacher::AttachEngine3D
  MapMode = 47
  Placement = pos=(-0.26869,31.198,-41.9178) rot=(0,0.91224,0.409656;3.14159rad)
  Support = -> [p_surf6,p_norm6,p_aux6]
FEATURE [PartDesign::Point] p_surf7
  AttacherType = Attacher::AttachEnginePoint
  Placement = pos=(47.1018,31.4599,0.385248) rot=(0,0,1;0rad)
FEATURE [PartDesign::Point] p_norm7
  AttacherType = Attacher::AttachEnginePoint
  Placement = pos=(47.6259,32.3115,0.385248) rot=(0,0,1;0rad)
FEATURE [PartDesign::Point] p_aux7
  AttacherType = Attacher::AttachEnginePoint
  Placement = pos=(46.1018,31.4599,0.385248) rot=(0,0,1;0rad)
FEATURE [PartDesign::CoordinateSystem] s_lcs7
  AttacherType = Attacher::AttachEngine3D
  MapMode = 47
  Placement = pos=(47.1018,31.4599,0.385248) rot=(0.196249,0.693356,0.693356;2.75402rad)
  Support = -> [p_surf7,p_norm7,p_aux7]
FEATURE [PartDesign::Point] p_surf8
  AttacherType = Attacher::AttachEnginePoint
  Placement = pos=(35.8327,33.6545,23.5859) rot=(0,0,1;0rad)
FEATURE [PartDesign::Point] p_norm8
  AttacherType = Attacher::AttachEnginePoint
  Placement = pos=(36.2335,34.4784,23.9867) rot=(0,0,1;0rad)
FEATURE [PartDesign::Point] p_aux8
  AttacherType = Attacher::AttachEnginePoint
  Placement = pos=(34.8327,33.6545,23.5859) rot=(0,0,1;0rad)
FEATURE [PartDesign::CoordinateSystem] s_lcs8
  AttacherType = Attacher::AttachEngine3D
  MapMode = 47
  Placement = pos=(35.8327,33.6545,23.5859) rot=(0.174608,0.522191,0.834763;2.924rad)
  Support = -> [p_surf8,p_norm8,p_aux8]
FEATURE [PartDesign::Point] p_surf9
  AttacherType = Attacher::AttachEnginePoint
  Placement = pos=(-47.9984,30.9792,-4.23481) rot=(0,0,1;0rad)
FEATURE [PartDesign::Point] p_norm9
  AttacherType = Attacher::AttachEnginePoint
  Placement = pos=(-48.4981,31.8401,-4.32964) rot=(0,0,1;0rad)
FEATURE [PartDesign::Point] p_aux9
  AttacherType = Attacher::AttachEnginePoint
  Placement = pos=(-48.9984,30.9792,-4.23481) rot=(0,0,1;0rad)
FEATURE [PartDesign::CoordinateSystem] s_lcs9
  AttacherType = Attacher::AttachEngine3D
  MapMode = 47
  Placement = pos=(-47.9984,30.9792,-4.23481) rot=(-0.175892,0.733193,0.656879;3.52931rad)
  Support = -> [p_surf9,p_norm9,p_aux9]
FEATURE [PartDesign::Point] p_surf10
  AttacherType = Attacher::AttachEnginePoint
  Placement = pos=(10.7488,6.06458,-43.2984) rot=(0,0,1;0rad)
FEATURE [PartDesign::Point] p_norm10
  AttacherType = Attacher::AttachEnginePoint
  Placement = pos=(10.7488,5.46458,-44.0984) rot=(0,0,1;0rad)
FEATURE [PartDesign::Body] Body  label="tracker-base"
  Group = -> [Sketch,DatumPlane,DatumPlane001,Sketch001,Sketch002,AdditiveLoft,Thickness,p_surf0,p_norm0,p_aux0,s_lcs0,p_surf1,p_norm1,p_aux1,s_lcs1,p_surf2,p_norm2,p_aux2,s_lcs2,p_surf3,p_norm3,p_aux3,s_lcs3,p_surf4,p_norm4,p_aux4,s_lcs4,p_surf5,p_norm5,p_aux5,s_lcs5,p_surf6,p_norm6,p_aux6,s_lcs6,p_surf7,p_norm7,p_aux7,s_lcs7,p_surf8,p_norm8,p_aux8,s_lcs8,p_surf9,p_norm9,p_aux9,s_lcs9,p_surf10,p_norm10,+10 more]
  Origin = -> Origin
  Placement = pos=(0,0,0) rot=(-1,0,0;1.5708rad)
  Tip = -> Thickness
COMPONENT P16 — same part as P15; its construction recipe is shown at P15.
PROVENANCE & LICENSES
A FreeCAD (.FCStd) document from a public repository crawl; recipes are the document's own serialized feature recipes (and, for linked parts, companion documents' recipes).
License: apache-2.0.
